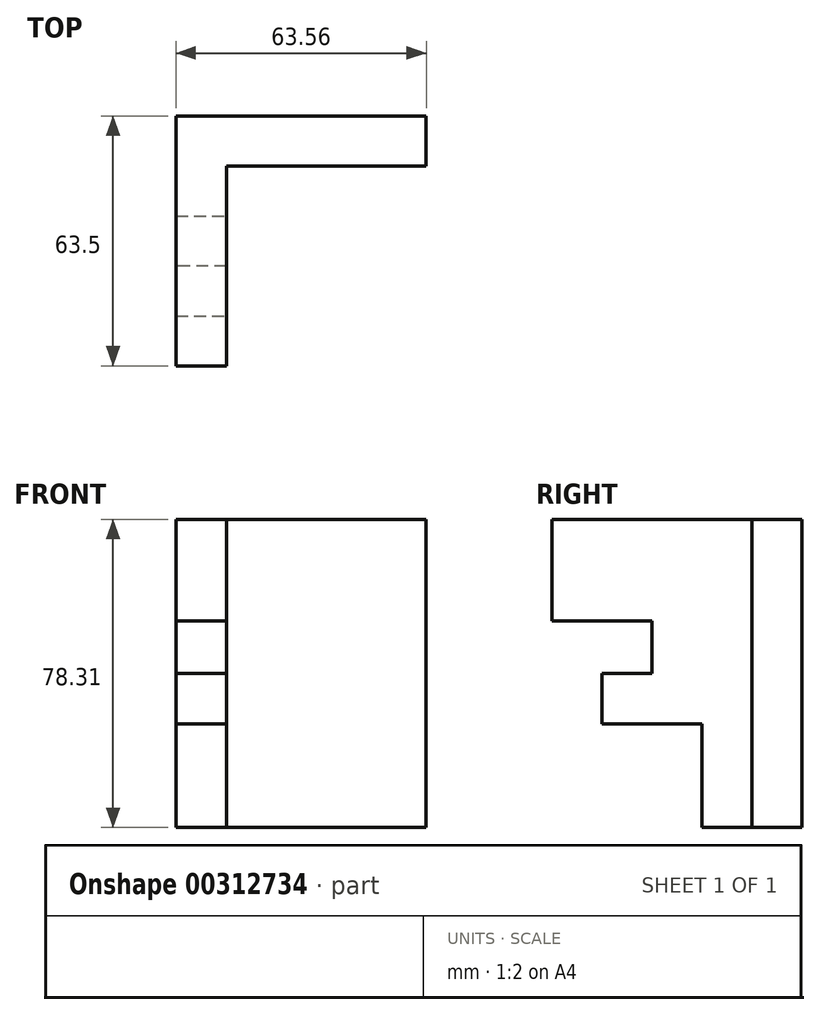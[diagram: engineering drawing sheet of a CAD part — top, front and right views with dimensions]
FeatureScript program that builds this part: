
annotation { "Feature Type Name" : "Feature", "Feature Type Description" : "" }
export const myFeature = defineFeature(function(context is Context, id is Id, definition is map)
    precondition{}
    {
        {
            var Q0;
            Q0=qCreatedBy(makeId("Front.planeOp"),FACE);
            var sketch = newSketch(context, id + "F0", { "sketchPlane" : qUnion([Q0])});
            skLineSegment(sketch, "E0", {"start": v(-41, -35.75) * mm, "end": v(22.56, -35.75) * mm});
            skLineSegment(sketch, "E1", {"start": v(22.56, -35.75) * mm, "end": v(22.56, 42.56) * mm});
            skLineSegment(sketch, "E2", {"start": v(22.56, 42.56) * mm, "end": v(-41, 42.56) * mm});
            skLineSegment(sketch, "E3", {"start": v(-41, 42.56) * mm, "end": v(-41, -35.75) * mm});
            skLineSegment(sketch, "E4", {"start": v(-41, 42.56) * mm, "end": v(-28.23, 42.56) * mm});
            skLineSegment(sketch, "E5", {"start": v(-28.23, 42.56) * mm, "end": v(-28.23, -35.75) * mm});
            skLineSegment(sketch, "E6", {"start": v(-28.23, -35.75) * mm, "end": v(-41, -35.75) * mm});
            skSolve(sketch);
        }
        {
            var Q0;
            Q0=makeQuery(id+"F0.imprint","IMPRINT",FACE,{"disambiguationData":[TD([[makeQuery(id+"F0.imprint","IMPRINT",EDGE,{"derivedFrom":sQuery(id+"F0.wireOp",EDGE,"E0")}),1.0]])]});
            extrude(context, id + "F1", {"entities" : qUnion([Q0]), "depth" : 12.7 * mm});
        }
        {
            var Q0;
            Q0=makeQuery(id+"F0.imprint","IMPRINT",FACE,{"disambiguationData":[TD([[makeQuery(id+"F0.imprint","IMPRINT",EDGE,{"derivedFrom":sQuery(id+"F0.wireOp",EDGE,"E3")}),1.0]])]});
            extrude(context, id + "F2", {"entities" : qUnion([Q0]), "operationType" : NewBodyOperationType.ADD, "depth" : 63.5 * mm});
        }
        {
            var Q0;
            Q0=makeQuery(id+"F2.opExtrude","CAP_FACE",FACE,{"disambiguationData":[OSD([sQuery(id+"F0.wireOp",EDGE,"E3"),sQuery(id+"F0.wireOp",EDGE,"E4"),sQuery(id+"F0.wireOp",EDGE,"E5"),sQuery(id+"F0.wireOp",EDGE,"E6")])],"isStart":false});
            var sketch = newSketch(context, id + "F3", { "sketchPlane" : qUnion([Q0])});
            skLineSegment(sketch, "E7", {"start": v(-28.23, 42.56) * mm, "end": v(-28.23, 16.74) * mm});
            skLineSegment(sketch, "E8", {"start": v(-28.23, 16.74) * mm, "end": v(-41, 16.74) * mm});
            skLineSegment(sketch, "E9", {"start": v(-41, 16.74) * mm, "end": v(-41, 3.4) * mm});
            skLineSegment(sketch, "E10", {"start": v(-41, 3.4) * mm, "end": v(-28.23, 3.4) * mm});
            skLineSegment(sketch, "E11", {"start": v(-28.23, 3.4) * mm, "end": v(-28.23, 16.74) * mm});
            skSolve(sketch);
        }
        {
            var Q0;
            Q0=makeQuery(id+"F3.imprint","IMPRINT",FACE,{"disambiguationData":[TD([[makeQuery(id+"F3.imprint","IMPRINT",EDGE,{"derivedFrom":sQuery(id+"F3.wireOp",EDGE,"E8")}),1.0]])]});
            extrude(context, id + "F4", {"entities" : qUnion([Q0]), "operationType" : NewBodyOperationType.REMOVE, "oppositeDirection" : true, "depth" : 25.4 * mm});
        }
        {
            var Q0;
            {var subQ0=sQuery(id+"F0.wireOp",EDGE,"E6");var subQ1=sQuery(id+"F0.wireOp",EDGE,"E3");var subQ2=sQuery(id+"F0.wireOp",EDGE,"E5");Q0=makeQuery(id+"F4.boolean.opBoolean","SPLIT",FACE,{"disambiguationData":[TD([makeQuery(id+"F1.opExtrude","SWEPT_FACE",FACE,{"disambiguationData":[OSD([sQuery(id+"F0.wireOp",EDGE,"E0")])]})])],"derivedFrom":makeQuery(id+"F2.opExtrude","CAP_FACE",FACE,{"disambiguationData":[OSD([subQ1,sQuery(id+"F0.wireOp",EDGE,"E4"),subQ2,subQ0])],"isStart":false})});}
            var sketch = newSketch(context, id + "F5", { "sketchPlane" : qUnion([Q0])});
            skLineSegment(sketch, "E12", {"start": v(-41, 3.4) * mm, "end": v(-28.23, 3.4) * mm});
            skLineSegment(sketch, "E13", {"start": v(-28.23, 3.4) * mm, "end": v(-28.23, -9.36) * mm});
            skLineSegment(sketch, "E14", {"start": v(-28.23, -9.36) * mm, "end": v(-41, -9.36) * mm});
            skLineSegment(sketch, "E15", {"start": v(-41, -9.36) * mm, "end": v(-41, 3.4) * mm});
            skSolve(sketch);
        }
        {
            var Q0;
            Q0=makeQuery(id+"F5.imprint","IMPRINT",FACE,{"disambiguationData":[TD([[makeQuery(id+"F5.imprint","IMPRINT",EDGE,{"derivedFrom":sQuery(id+"F5.wireOp",EDGE,"E12")}),-1.0]])]});
            extrude(context, id + "F6", {"entities" : qUnion([Q0]), "operationType" : NewBodyOperationType.REMOVE, "oppositeDirection" : true, "depth" : 12.7 * mm});
        }
        {
            var Q0;
            {var subQ0=sQuery(id+"F0.wireOp",EDGE,"E6");var subQ1=sQuery(id+"F0.wireOp",EDGE,"E3");var subQ2=sQuery(id+"F0.wireOp",EDGE,"E5");Q0=makeQuery(id+"F4.boolean.opBoolean","SPLIT",FACE,{"disambiguationData":[TD([makeQuery(id+"F1.opExtrude","SWEPT_FACE",FACE,{"disambiguationData":[OSD([sQuery(id+"F0.wireOp",EDGE,"E0")])]})])],"derivedFrom":makeQuery(id+"F2.opExtrude","CAP_FACE",FACE,{"disambiguationData":[OSD([subQ1,sQuery(id+"F0.wireOp",EDGE,"E4"),subQ2,subQ0])],"isStart":false})});}
            extrude(context, id + "F7", {"entities" : qUnion([Q0]), "operationType" : NewBodyOperationType.REMOVE, "oppositeDirection" : true, "depth" : 38.1 * mm});
        }
    });
